# Revit family: PCI
name_source: partatom
category: Air Terminals
revit_build: Autodesk Revit MEP 2012 (Build: 20110309_2315(x64)
units: mm (PartAtom-declared; Revit-internal decimal feet)

## types (12) — shared parameters
Manufacturer = INNES
Material malla = Aluminio/Fierro
Minima presión estática = 0.02 in-wg
Máxima presión estática = 0.22 in-wg
Plato = 23 3/4"
URL = http://www.innes.com.mx
calibre = 1/8"

## per-type parameters (varying)
| type | A | AI | Cuello | Cuello cuadrado | Cuello redondo | Max Flow | Min Flow | Minima velocidad de cuello | Máxima velocidad de cuello | Máximo nivel de ruido (NC) | Radio | RadioI |
| PCI-R-06-24 | 6" | 5 3/4" | Redondo | No | Yes | 175 CFM | 60 CFM | 300 FPM | 900 FPM | 39 | 3" | 2 7/8" |
| PCI-R-08-24 | 8" | 7 3/4" | Redondo | No | Yes | 315 CFM | 105 CFM | 300 FPM | 900 FPM | 42 | 4" | 3 7/8" |
| PCI-R-10-24 | 10" | 9 3/4" | Redondo | No | Yes | 490 CFM | 165 CFM | 300 FPM | 900 FPM | 44 | 5" | 4 7/8" |
| PCI-R-12-24 | 12" | 11 3/4" | Redondo | No | Yes | 705 CFM | 235 CFM | 300 FPM | 900 FPM | 46 | 6" | 5 7/8" |
| PCI-R-14-24 | 14" | 13 3/4" | Redondo | No | Yes | 960 CFM | 320 CFM | 300 FPM | 900 FPM | 49 | 7" | 6 7/8" |
| PCI-R-16-24 | 16" | 15 3/4" | Redondo | No | Yes | 1100 CFM | 370 CFM | 300 FPM | 900 FPM | 51 | 8" | 7 7/8" |
| PCI-C-06-24 | 6" | 5 3/4" | Cuadrado | Yes | No | 175 CFM | 60 CFM | 300 FPM | 900 FPM | 39 | 3" | 2 7/8" |
| PCI-C-08-24 | 8" | 7 3/4" | Cuadrado | Yes | No | 315 CFM | 105 CFM | 300 FPM | 900 FPM | 42 | 4" | 3 7/8" |
| PCI-C-10-24 | 10" | 9 3/4" | Cuadrado | Yes | No | 490 CFM | 165 CFM | 300 FPM | 900 FPM | 44 | 5" | 4 7/8" |
| PCI-C-12-24 | 12" | 11 3/4" | Cuadrado | Yes | No | 705 CFM | 235 CFM | 300 FPM | 900 FPM | 46 | 6" | 5 7/8" |
| PCI-C-14-24 | 14" | 13 3/4" | Cuadrado | Yes | No | 1100 CFM | 320 CFM | 300 FPM | 900 FPM | 49 | 7" | 6 7/8" |
| PCI-C-15-24 | 15" | 14 3/4" | Cuadrado | Yes | No | 0 CFM | 0 CFM | 0 FPM | 0 FPM | 0 | 7 1/2" | 7 3/8" |

## geometry (parser evidence)
native form markers: Blend x15, Sweep x1
no freeform markers — native parametric forms only
